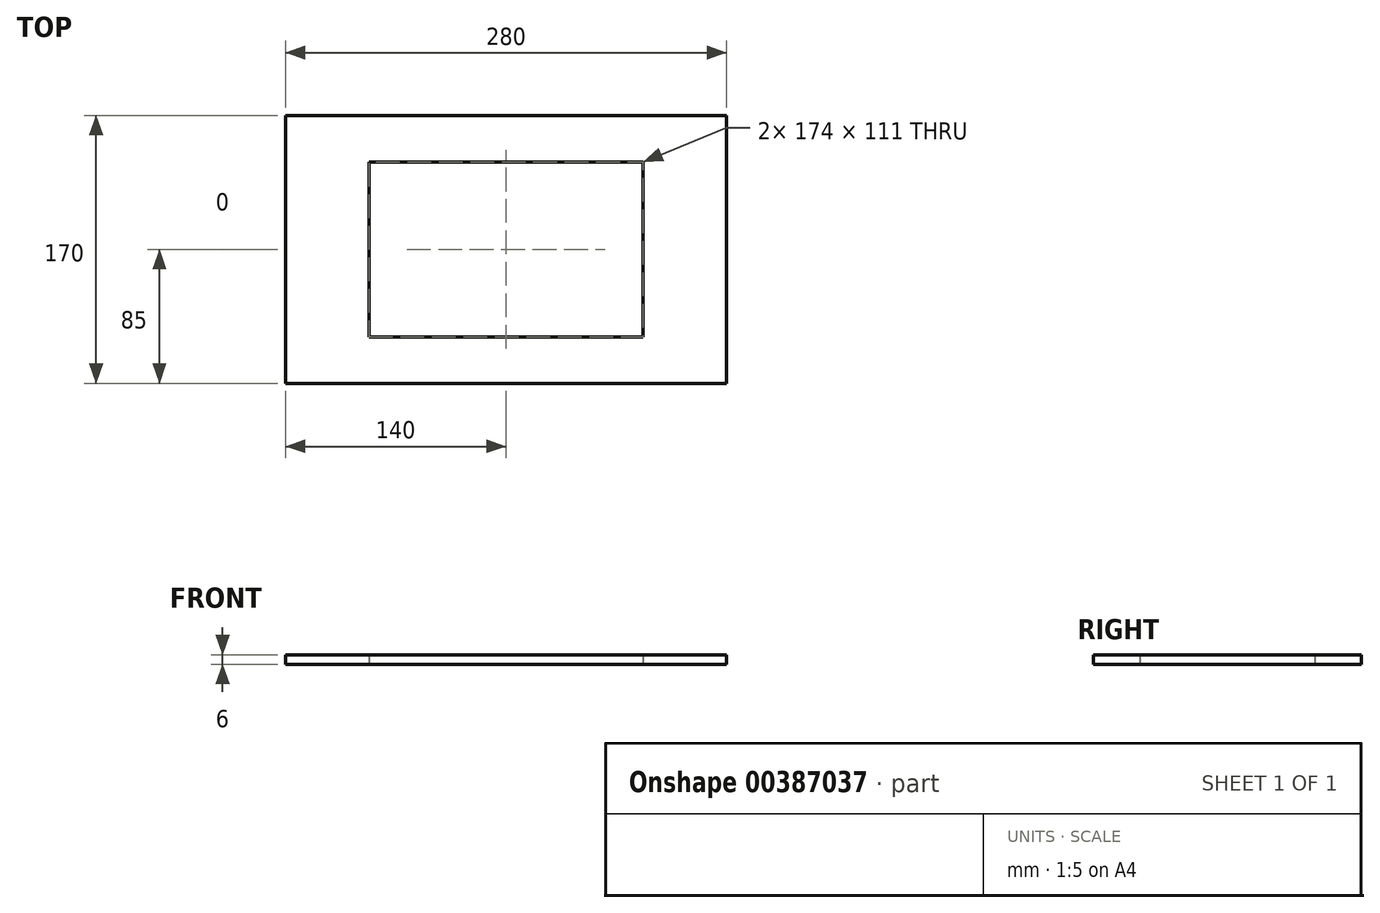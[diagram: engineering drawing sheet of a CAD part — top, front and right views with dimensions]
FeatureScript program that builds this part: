
annotation { "Feature Type Name" : "Feature", "Feature Type Description" : "" }
export const myFeature = defineFeature(function(context is Context, id is Id, definition is map)
    precondition{}
    {
        {
            var Q0;
            Q0=qCreatedBy(makeId("Top.planeOp"),FACE);
            var sketch = newSketch(context, id + "F0", { "sketchPlane" : qUnion([Q0])});
            skLineSegment(sketch, "E0.bottom", {"start": v(140, 85) * mm, "end": v(-140, 85) * mm});
            skLineSegment(sketch, "E0.top", {"start": v(140, -85) * mm, "end": v(-140, -85) * mm});
            skLineSegment(sketch, "E0.left", {"start": v(140, 85) * mm, "end": v(140, -85) * mm});
            skLineSegment(sketch, "E0.right", {"start": v(-140, 85) * mm, "end": v(-140, -85) * mm});
            skPoint(sketch, "E0.middle", {"position": v(0, 0) * mm});
            skLineSegment(sketch, "E1.bottom", {"start": v(87, 55.5) * mm, "end": v(-87, 55.5) * mm});
            skLineSegment(sketch, "E1.top", {"start": v(87, -55.5) * mm, "end": v(-87, -55.5) * mm});
            skLineSegment(sketch, "E1.left", {"start": v(87, 55.5) * mm, "end": v(87, -55.5) * mm});
            skLineSegment(sketch, "E1.right", {"start": v(-87, 55.5) * mm, "end": v(-87, -55.5) * mm});
            skSolve(sketch);
        }
        {
            var Q0;
            Q0=makeQuery(id+"F0.imprint","IMPRINT",FACE,{"disambiguationData":[TD([[makeQuery(id+"F0.imprint","IMPRINT",EDGE,{"derivedFrom":sQuery(id+"F0.wireOp",EDGE,"E0.bottom")}),1.0]])]});
            extrude(context, id + "F1", {"entities" : qUnion([Q0]), "depth" : 6 * mm});
        }
    });
